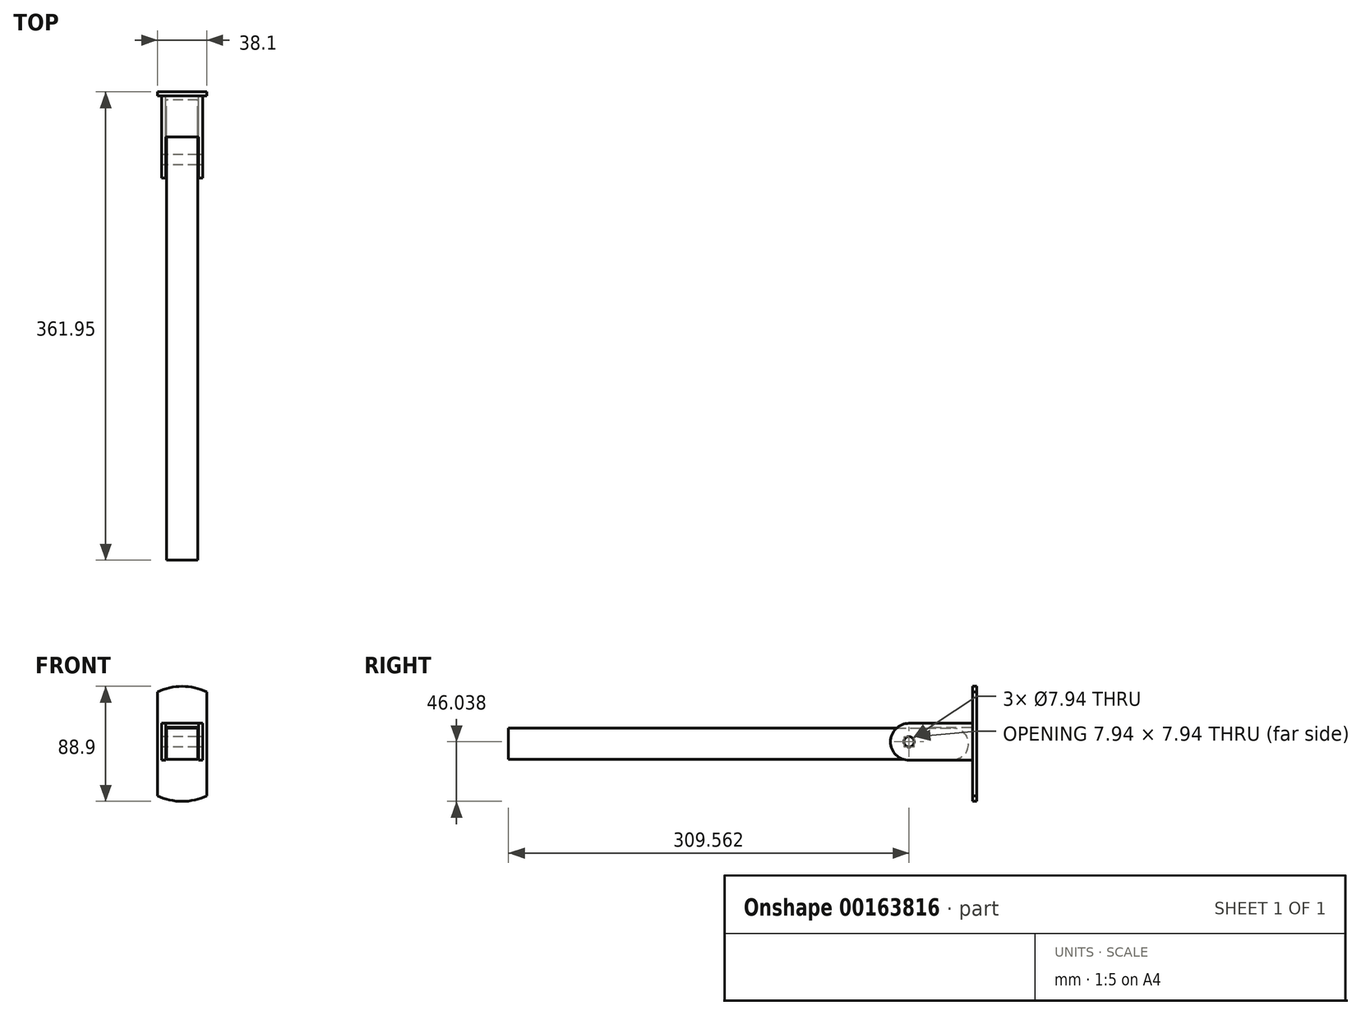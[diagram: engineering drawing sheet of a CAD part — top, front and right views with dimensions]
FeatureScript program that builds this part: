
annotation { "Feature Type Name" : "Feature", "Feature Type Description" : "" }
export const myFeature = defineFeature(function(context is Context, id is Id, definition is map)
    precondition{}
    {
        {
            var Q0;
            Q0=qCreatedBy(makeId("Front.planeOp"),FACE);
            var sketch = newSketch(context, id + "F0", { "sketchPlane" : qUnion([Q0])});
            skArc(sketch, "E0", {"start": v(-19.05, -40.16) * mm, "mid": v(0, -44.45) * mm, "end": v(19.05, -40.16) * mm});
            skLineSegment(sketch, "E1.left", {"start": v(19.05, 40.16) * mm, "end": v(19.05, -40.16) * mm});
            skLineSegment(sketch, "E1.right", {"start": v(-19.05, 40.16) * mm, "end": v(-19.05, -40.16) * mm});
            skArc(sketch, "E2.trimOffspring", {"start": v(19.05, 40.16) * mm, "mid": v(0, 44.45) * mm, "end": v(-19.05, 40.16) * mm});
            skSolve(sketch);
        }
        {
            var Q0;
            Q0=makeQuery(id+"F0.imprint","IMPRINT",FACE,{"disambiguationData":[TD([[makeQuery(id+"F0.imprint","IMPRINT",EDGE,{"derivedFrom":sQuery(id+"F0.wireOp",EDGE,"E0")}),1.0]])]});
            extrude(context, id + "F1", {"entities" : qUnion([Q0]), "depth" : 3.17 * mm});
        }
        {
            var Q0;
            Q0=makeQuery(id+"F1.opExtrude","CAP_FACE",FACE,{"disambiguationData":[OSD([sQuery(id+"F0.wireOp",EDGE,"E0"),sQuery(id+"F0.wireOp",EDGE,"E1.left"),sQuery(id+"F0.wireOp",EDGE,"E1.right"),sQuery(id+"F0.wireOp",EDGE,"E2.trimOffspring")])],"isStart":false});
            var sketch = newSketch(context, id + "F2", { "sketchPlane" : qUnion([Q0])});
            skLineSegment(sketch, "E3.bottom", {"start": v(12.7, 12.7) * mm, "end": v(-12.7, 12.7) * mm});
            skLineSegment(sketch, "E3.left", {"start": v(12.7, 12.7) * mm, "end": v(12.7, -12.7) * mm});
            skLineSegment(sketch, "E3.right", {"start": v(-12.7, 12.7) * mm, "end": v(-12.7, -12.7) * mm});
            skPoint(sketch, "E3.middle", {"position": v(0, 0) * mm});
            skLineSegment(sketch, "E4.0", {"start": v(-15.88, 15.88) * mm, "end": v(-15.88, -12.7) * mm});
            skLineSegment(sketch, "E4.1", {"start": v(15.87, 15.88) * mm, "end": v(-15.88, 15.88) * mm});
            skLineSegment(sketch, "E4.2", {"start": v(15.87, 15.88) * mm, "end": v(15.88, -12.7) * mm});
            skLineSegment(sketch, "E5", {"start": v(-15.88, -12.7) * mm, "end": v(-12.7, -12.7) * mm});
            skLineSegment(sketch, "E6.trimOffspring", {"start": v(12.7, -12.7) * mm, "end": v(15.88, -12.7) * mm});
            skSolve(sketch);
        }
        {
            var Q0;
            Q0=makeQuery(id+"F2.imprint","IMPRINT",FACE,{"disambiguationData":[TD([[makeQuery(id+"F2.imprint","IMPRINT",EDGE,{"derivedFrom":sQuery(id+"F2.wireOp",EDGE,"E3.bottom")}),-1.0]])]});
            extrude(context, id + "F3", {"entities" : qUnion([Q0]), "operationType" : NewBodyOperationType.ADD, "depth" : 31.75 * mm});
        }
        {
            var Q0;
            Q0=makeQuery(id+"F3.opExtrude","CAP_FACE",FACE,{"disambiguationData":[OSD([sQuery(id+"F2.wireOp",EDGE,"E3.bottom"),sQuery(id+"F2.wireOp",EDGE,"E3.left"),sQuery(id+"F2.wireOp",EDGE,"E3.right"),sQuery(id+"F2.wireOp",EDGE,"E4.0"),sQuery(id+"F2.wireOp",EDGE,"E4.1"),sQuery(id+"F2.wireOp",EDGE,"E4.2"),sQuery(id+"F2.wireOp",EDGE,"E5"),sQuery(id+"F2.wireOp",EDGE,"E6.trimOffspring")])],"isStart":false});
            var sketch = newSketch(context, id + "F4", { "sketchPlane" : qUnion([Q0])});
            skLineSegment(sketch, "E7.0.1", {"start": v(12.7, 15.88) * mm, "end": v(12.7, -12.7) * mm});
            skLineSegment(sketch, "E7.0.2", {"start": v(12.7, -12.7) * mm, "end": v(15.88, -12.7) * mm});
            skLineSegment(sketch, "E7.0.3", {"start": v(15.88, -12.7) * mm, "end": v(15.87, 15.88) * mm});
            skLineSegment(sketch, "E7.0.4", {"start": v(15.87, 15.88) * mm, "end": v(12.7, 15.88) * mm});
            skLineSegment(sketch, "E7.0.5", {"start": v(-15.88, 15.88) * mm, "end": v(-15.88, -12.7) * mm});
            skLineSegment(sketch, "E7.0.6", {"start": v(-15.88, -12.7) * mm, "end": v(-12.7, -12.7) * mm});
            skLineSegment(sketch, "E7.0.7", {"start": v(-12.7, -12.7) * mm, "end": v(-12.7, 15.88) * mm});
            skPoint(sketch, "E7.0.0.end.orphan", {"position": v(12.7, 12.7) * mm});
            skPoint(sketch, "E7.0.0.start.orphan", {"position": v(-12.7, 12.7) * mm});
            skLineSegment(sketch, "E8.trimOffspring", {"start": v(-12.7, 15.88) * mm, "end": v(-15.88, 15.88) * mm});
            skSolve(sketch);
        }
        {
            var Q0;
            Q0=makeQuery(id+"F4.imprint","IMPRINT",FACE,{"disambiguationData":[TD([[makeQuery(id+"F4.imprint","IMPRINT",EDGE,{"derivedFrom":sQuery(id+"F4.wireOp",EDGE,"E7.0.5")}),1.0]])]});
            var Q1;
            {var subQ2=sQuery(id+"F4.wireOp",EDGE,"E7.0.2");Q1=makeQuery(id+"F4.imprint","IMPRINT",FACE,{"disambiguationData":[TD([[makeQuery(id+"F4.imprint","IMPRINT",EDGE,{"derivedFrom":subQ2}),1.0]])]});}
            extrude(context, id + "F5", {"entities" : qUnion([Q0, Q1]), "operationType" : NewBodyOperationType.ADD, "depth" : 31.75 * mm});
        }
        {
            var Q0;
            Q0=makeQuery(id+"F5.opExtrude","CAP_EDGE",EDGE,{"disambiguationData":[OSD([sQuery(id+"F4.wireOp",EDGE,"E8.trimOffspring")])],"isStart":false});
            var Q1;
            Q1=makeQuery(id+"F5.opExtrude","CAP_EDGE",EDGE,{"disambiguationData":[OSD([sQuery(id+"F4.wireOp",EDGE,"E7.0.6")])],"isStart":false});
            var Q2;
            Q2=makeQuery(id+"F5.opExtrude","CAP_EDGE",EDGE,{"disambiguationData":[OSD([sQuery(id+"F4.wireOp",EDGE,"E7.0.2")])],"isStart":false});
            var Q3;
            Q3=makeQuery(id+"F5.opExtrude","CAP_EDGE",EDGE,{"disambiguationData":[OSD([sQuery(id+"F4.wireOp",EDGE,"E7.0.4")])],"isStart":false});
            fillet(context, id + "F6", {"entities" : qUnion([Q0, Q1, Q2, Q3]), "radius" : 14.29 * mm, "tangentPropagation" : true, "allowEdgeOverflow" : false});
        }
        {
            var Q0;
            Q0=makeQuery(id+"F5.boolean.opBoolean","MERGE",FACE,{"derivedFrom":[makeQuery(id+"F3.opExtrude","SWEPT_FACE",FACE,{"disambiguationData":[OSD([sQuery(id+"F2.wireOp",EDGE,"E4.0")])]}),makeQuery(id+"F5.opExtrude","SWEPT_FACE",FACE,{"disambiguationData":[OSD([sQuery(id+"F4.wireOp",EDGE,"E7.0.5")])]})]});
            var sketch = newSketch(context, id + "F7", { "sketchPlane" : qUnion([Q0])});
            skPoint(sketch, "E9", {"position": v(52.39, 1.59) * mm});
            skSolve(sketch);
        }
        {
            var Q0;
            Q0=sQuery(id+"F7.wireOp",VERTEX,"E9");
            var Q1;
            Q1=makeQuery(id+"F1.opExtrude","SWEPT_BODY",BODY,{"disambiguationData":[OSD([sQuery(id+"F0.wireOp",EDGE,"E0"),sQuery(id+"F0.wireOp",EDGE,"E1.left"),sQuery(id+"F0.wireOp",EDGE,"E1.right"),sQuery(id+"F0.wireOp",EDGE,"E2.trimOffspring")])]});
            hole(context, id + "F8", {"style" : HoleStyle.SIMPLE, "endStyle" : HoleEndStyle.BLIND, "holeDiameter" : 7.94 * mm, "holeDepth" : 50.8 * mm, "startFromSketch" : true, "locations" : qUnion([Q0]), "scope" : qUnion([Q1])});
        }
        {
            var Q0;
            Q0=makeQuery(id+"F1.opExtrude","CAP_FACE",FACE,{"disambiguationData":[OSD([sQuery(id+"F0.wireOp",EDGE,"E0"),sQuery(id+"F0.wireOp",EDGE,"E1.left"),sQuery(id+"F0.wireOp",EDGE,"E1.right"),sQuery(id+"F0.wireOp",EDGE,"E2.trimOffspring")])],"isStart":false});
            cPlane(context, id + "F9", {"entities" : qUnion([Q0]), "cplaneType" : CPlaneType.OFFSET, "offset" : 3.17 * mm, "width" : 152.4 * mm, "height" : 152.4 * mm});
        }
        {
            var Q0;
            Q0=qCreatedBy(id+"F9.planeOp",FACE);
            var sketch = newSketch(context, id + "F10", { "sketchPlane" : qUnion([Q0])});
            skLineSegment(sketch, "E10.bottom", {"start": v(12.07, 12.07) * mm, "end": v(-12.07, 12.07) * mm});
            skLineSegment(sketch, "E10.top", {"start": v(12.07, -12.07) * mm, "end": v(-12.07, -12.07) * mm});
            skLineSegment(sketch, "E10.left", {"start": v(12.07, 12.07) * mm, "end": v(12.07, -12.07) * mm});
            skLineSegment(sketch, "E10.right", {"start": v(-12.07, 12.07) * mm, "end": v(-12.07, -12.07) * mm});
            skPoint(sketch, "E10.middle", {"position": v(0, 0) * mm});
            skSolve(sketch);
        }
        {
            var Q0;
            Q0=makeQuery(id+"F10.imprint","IMPRINT",FACE,{"disambiguationData":[TD([[makeQuery(id+"F10.imprint","IMPRINT",EDGE,{"derivedFrom":sQuery(id+"F10.wireOp",EDGE,"E10.bottom")}),1.0]])]});
            extrude(context, id + "F11", {"entities" : qUnion([Q0]), "depth" : 355.6 * mm});
        }
        {
            var Q0;
            Q0=makeQuery(id+"F11.opExtrude","SWEPT_FACE",FACE,{"disambiguationData":[OSD([sQuery(id+"F10.wireOp",EDGE,"E10.right")])]});
            var sketch = newSketch(context, id + "F12", { "sketchPlane" : qUnion([Q0])});
            skPoint(sketch, "E11", {"position": v(52.39, 1.59) * mm});
            skSolve(sketch);
        }
        {
            var Q0;
            Q0=sQuery(id+"F12.wireOp",VERTEX,"E11");
            var Q1;
            Q1=makeQuery(id+"F11.opExtrude","SWEPT_BODY",BODY,{"disambiguationData":[OSD([sQuery(id+"F10.wireOp",EDGE,"E10.bottom"),sQuery(id+"F10.wireOp",EDGE,"E10.top"),sQuery(id+"F10.wireOp",EDGE,"E10.left"),sQuery(id+"F10.wireOp",EDGE,"E10.right")])]});
            hole(context, id + "F13", {"style" : HoleStyle.SIMPLE, "endStyle" : HoleEndStyle.BLIND, "holeDiameter" : 7.94 * mm, "holeDepth" : 50.8 * mm, "startFromSketch" : true, "locations" : qUnion([Q0]), "scope" : qUnion([Q1])});
        }
        {
            var Q0;
            Q0=makeQuery(id+"F11.opExtrude","CAP_EDGE",EDGE,{"disambiguationData":[OSD([sQuery(id+"F10.wireOp",EDGE,"E10.bottom")])],"isStart":true});
            var Q1;
            Q1=makeQuery(id+"F11.opExtrude","CAP_EDGE",EDGE,{"disambiguationData":[OSD([sQuery(id+"F10.wireOp",EDGE,"E10.top")])],"isStart":true});
            fillet(context, id + "F14", {"entities" : qUnion([Q0, Q1]), "radius" : 12.06 * mm, "tangentPropagation" : true, "allowEdgeOverflow" : false});
        }
    });
